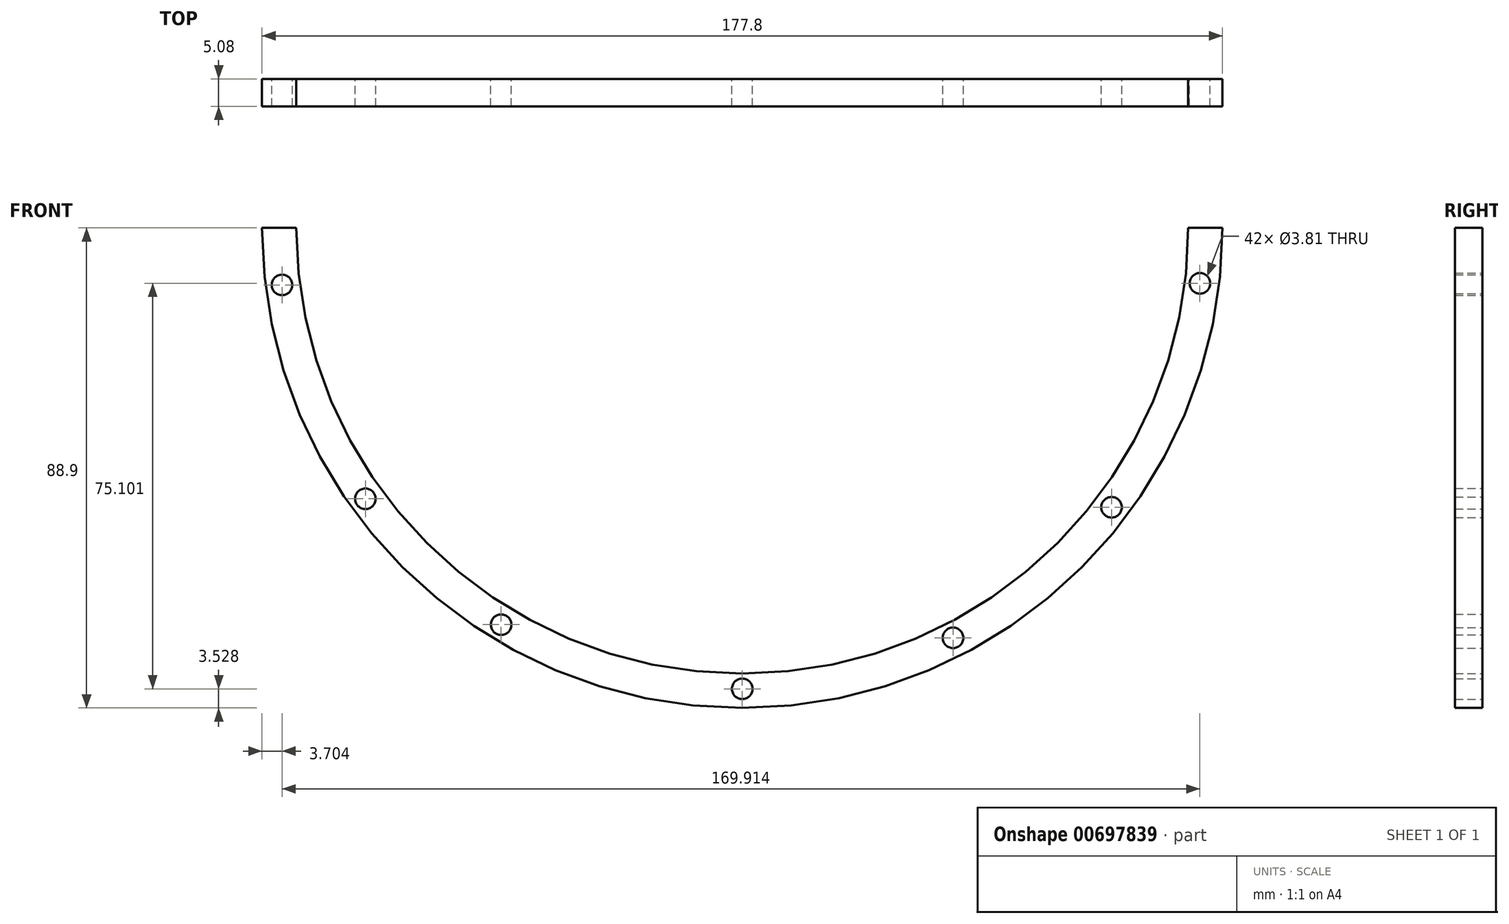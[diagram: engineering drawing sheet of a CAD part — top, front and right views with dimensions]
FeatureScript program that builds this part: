
annotation { "Feature Type Name" : "Feature", "Feature Type Description" : "" }
export const myFeature = defineFeature(function(context is Context, id is Id, definition is map)
    precondition{}
    {
        {
            var Q0;
            Q0=qCreatedBy(makeId("Front.planeOp"),FACE);
            var sketch = newSketch(context, id + "F0", { "sketchPlane" : qUnion([Q0])});
            skArc(sketch, "E0", {"start": v(-88.9, 0) * mm, "mid": v(0, -88.9) * mm, "end": v(88.9, 0) * mm});
            skArc(sketch, "E1", {"start": v(-82.55, 0) * mm, "mid": v(0, -82.55) * mm, "end": v(82.55, 0) * mm});
            skLineSegment(sketch, "E2", {"start": v(-88.9, 0) * mm, "end": v(-82.55, 0) * mm});
            skLineSegment(sketch, "E3.trimOffspring", {"start": v(82.55, 0) * mm, "end": v(88.9, 0) * mm});
            skCircle(sketch, "E4", {"center": v(-85.2, -10.57) * mm, "radius": 1.9 * mm});
            skCircle(sketch, "E5", {"center": v(-69.77, -50.18) * mm, "radius": 1.9 * mm});
            skCircle(sketch, "E6", {"center": v(-44.64, -73.49) * mm, "radius": 1.9 * mm});
            skCircle(sketch, "E7", {"center": v(0, -85.37) * mm, "radius": 1.9 * mm});
            skCircle(sketch, "E8", {"center": v(39.01, -75.93) * mm, "radius": 1.9 * mm});
            skCircle(sketch, "E9", {"center": v(68.36, -51.74) * mm, "radius": 1.9 * mm});
            skCircle(sketch, "E10", {"center": v(84.72, -10.27) * mm, "radius": 1.9 * mm});
            skSolve(sketch);
        }
        {
            var Q0;
            Q0 = qSketchRegion(id + "F0", true);
            extrude(context, id + "F1", {"entities" : qUnion([Q0]), "depth" : 5.08 * mm, "offsetDistance" : 25.4 * mm});
        }
    });
